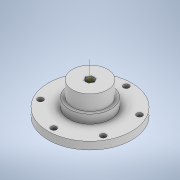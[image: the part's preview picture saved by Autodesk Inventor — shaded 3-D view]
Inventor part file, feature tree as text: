
AUTODESK INVENTOR PART (.ipt)
format: ipt  version: 2020 (Build 240168000, 168)  size: 148,992 bytes
history: native  units: in
note: dims shown in document units (in); Inventor stores cm internally (conversion verified against a paired STEP export)
features: sketch x6, extrude x5, other x1, pattern_circular x1
ambient origin geometry x8: Origin, YZ Plane, XZ Plane, XY Plane, X Axis, Y Axis, Z Axis, Center Point
bodies: Solid1 (feature_tree)
feature tree (13):
  extrude  "Extrusion1"  Depth=0.2in TaperAngle=0.0deg
  extrude  "Extrusion2"  Depth=0.23in TaperAngle=0.0deg
  extrude  "Extrusion3"  Depth=0.4in TaperAngle=0.0deg
  extrude  "Extrusion4"  Depth=1.0in TaperAngle=0.0deg
  extrude  "Extrusion5"  Depth=0.075in
  sketch  "Sketch7"  dims[d15=1.0in d16=0.0in d17=2.3622in d18=360.0deg]
  other  "Work Axis1"
  pattern_circular  "Circular Pattern1"  Count=6 Angle=360.0deg
  sketch  "Sketch1"  dims[d0=2.2in d1=0.2in d2=0.0in]
  sketch  "Sketch2"  dims[d3=1.1in d4=0.23in d5=0.0in]
  sketch  "Sketch3"  dims[d6=0.93in d7=0.4in d8=0.0in]
  sketch  "Sketch5"  dims[d10=0.105in d11=1.0in d12=0.0in]
  sketch  "Sketch6"  dims[d13=0.07in d14=0.075in]
